# Revit family: Keilhauer_Pact_Lounge Seating_77001
name_source: partatom
category: Furniture
revit_build: Autodesk Revit 2017 (Build: 20160225_1515(x64)
units: mm (PartAtom-declared; Revit-internal decimal feet)

## family parameters
Always vertical = Yes
Cut with Voids When Loaded = No
OmniClass Number = 23.40.70.14.64.11
OmniClass Title = Office Furniture
Room Calculation Point = No
Shared = No
Work Plane-Based = No

## types (3) — shared parameters
Assembly Code = E2020200
Catalog = Pact
Manufacturer = Keilhauer, Corp.
Product Documentation Link = http://www.keilhauer.com
URL = http://www.keilhauer.com

## per-type parameters (varying)
| type | Caster | Description | Flat Base | Glide | Mobile Base | Model | Type |
| 4-star Base with Glides | No | Chair with a 4-star base with glides and tablet | No | Yes | Yes | 77002 | 3 |
| 4-star Base with Casters | Yes | Chair with a 4-star base with casters and tablet | No | No | Yes | 77001 | 2 |
| Flat Base | No | Chair with a flat base and tablet | Yes | No | No | 77000 | 1 |

## geometry (parser evidence)
native form markers: Sweep x3
no freeform markers — native parametric forms only
